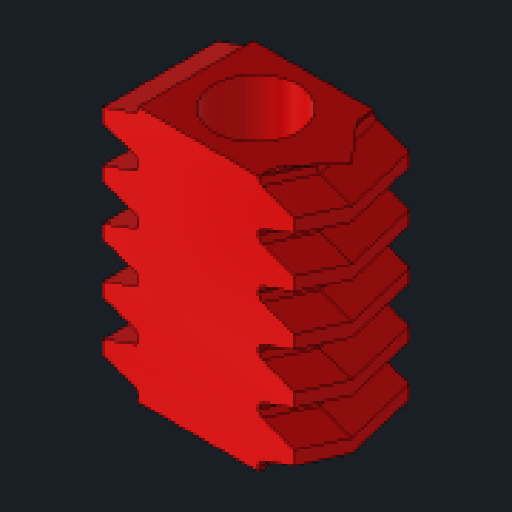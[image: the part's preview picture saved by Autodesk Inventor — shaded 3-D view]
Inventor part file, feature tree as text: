
AUTODESK INVENTOR PART (.ipt)
format: ipt  version: 2023.2 (Build 272271030, 271C)  size: 550,400 bytes
history: native  units: mm
features: sketch x4, projected_geometry x3, extrude x2, plane x2, pattern_linear x2, sweep x1, mirror x1, hole x1
ambient origin geometry x8: Origin, YZ Plane, XZ Plane, XY Plane, X Axis, Y Axis, Z Axis, Center Point
bodies: Solid1 (feature_tree)
feature tree (16):
  extrude  "Extrusion1"  Depth=20.0mm
  sketch  "Sketch2"  dims[d2=4.5mm d3=0.0mm d14=12.217305mm]
  plane  "Work Plane1"
  sweep  "Sweep1"
  pattern_linear  "Rectangular Pattern2"  Spacing1=2.8125mm  [1 undecoded]
  mirror  "Mirror2"
  extrude  "Extrusion3"  Depth=14.5mm
  pattern_linear  "Rectangular Pattern3"  Spacing1=1.963495mm  [1 undecoded]
  hole  "Hole1"  [1 undecoded]
  plane  "Work Plane2"
  sketch  "Sketch1"  dims[d0=14.5mm d1=20.0mm]
  projected_geometry  "Projected Loop1"
  sketch  "Sketch3"  dims[d15=22.5deg]
  projected_geometry  "Projected Loop2"
  sketch  "Sketch5"  dims[d16=0.475mm d17=2.8125mm d18=1.25mm d19=1.963495mm d20=-1.25mm d22=0.0mm d23=0.0mm d27=80.0mm d29=3.927mm d31=3.054326mm d32=3.577925mm d33=0.0mm d34=0.0mm d35=100.0mm d37=3.927mm d38=14.5mm d39=7.5mm d40=6.5mm d41=6.0mm d42=4.0mm d43=2.0mm d44=90.0deg d45=8.0mm d46=20.594885mm d47=-1.25mm d48=0.5mm d49=0.872665mm d50=0.5mm d51=0.872665mm]
  projected_geometry  "Projected Loop4"
note: 3 required parameter values undecoded (feature->parameter linkage not recoverable at this tier; creation-order binding heuristic only, values carry confidence <= 0.55)
